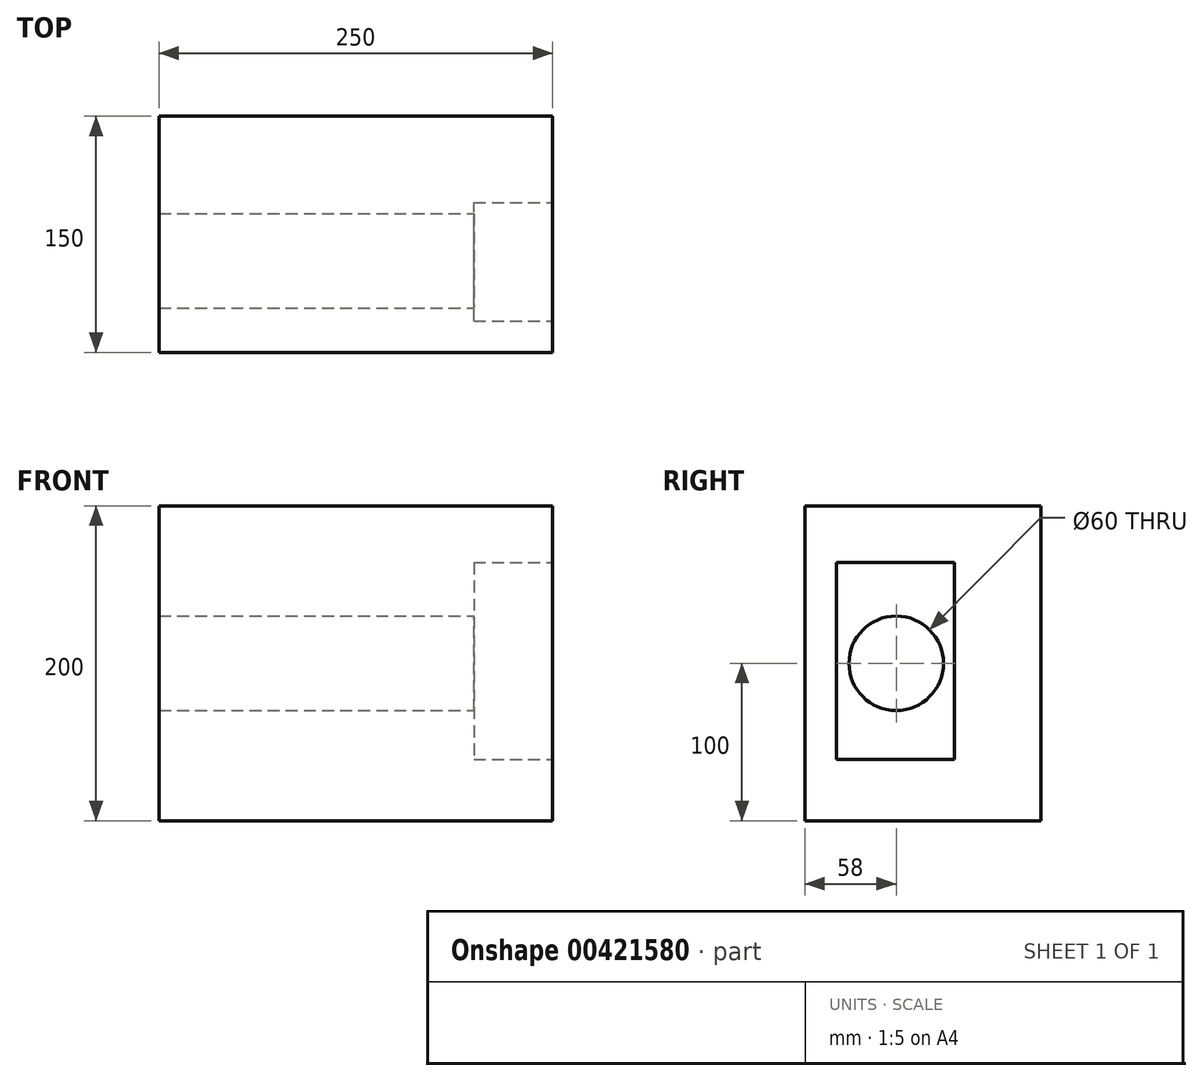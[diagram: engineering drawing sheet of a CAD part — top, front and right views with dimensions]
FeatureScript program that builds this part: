
annotation { "Feature Type Name" : "Feature", "Feature Type Description" : "" }
export const myFeature = defineFeature(function(context is Context, id is Id, definition is map)
    precondition{}
    {
        {
            var Q0;
            Q0=qCreatedBy(makeId("Front.planeOp"),FACE);
            var sketch = newSketch(context, id + "F0", { "sketchPlane" : qUnion([Q0])});
            skLineSegment(sketch, "E0.bottom", {"start": v(0, -31.1) * mm, "end": v(127.68, -31.1) * mm});
            skLineSegment(sketch, "E0.top", {"start": v(0, -82.4) * mm, "end": v(127.68, -82.4) * mm});
            skLineSegment(sketch, "E0.left", {"start": v(0, -31.1) * mm, "end": v(0, -82.4) * mm});
            skLineSegment(sketch, "E0.right", {"start": v(127.68, -31.1) * mm, "end": v(127.68, -82.4) * mm});
            skPoint(sketch, "E0.middle", {"position": v(63.84, -56.75) * mm});
            skSolve(sketch);
        }
        {
            var Q0;
            Q0=makeQuery(id+"F0.imprint","IMPRINT",FACE,{"disambiguationData":[TD([[makeQuery(id+"F0.imprint","IMPRINT",EDGE,{"derivedFrom":sQuery(id+"F0.wireOp",EDGE,"E0.bottom")}),-1.0]])]});
            extrude(context, id + "F1", {"entities" : qUnion([Q0]), "depth" : 114.37 * mm});
        }
        {
            var Q0;
            Q0=qCreatedBy(makeId("Front.planeOp"),FACE);
            var sketch = newSketch(context, id + "F2", { "sketchPlane" : qUnion([Q0])});
            skLineSegment(sketch, "E1", {"start": v(45.96, 141.6) * mm, "end": v(45.96, 90.77) * mm});
            skLineSegment(sketch, "E2", {"start": v(45.96, 90.77) * mm, "end": v(161.83, 90.77) * mm});
            skLineSegment(sketch, "E3", {"start": v(161.83, 90.77) * mm, "end": v(161.83, 141.6) * mm});
            skLineSegment(sketch, "E4", {"start": v(161.83, 141.6) * mm, "end": v(45.96, 141.6) * mm});
            skSolve(sketch);
        }
        {
            var Q0;
            Q0 = qSketchRegion(id + "F2", true);
            extrude(context, id + "F3", {"entities" : qUnion([Q0]), "depth" : 25 * mm, "offsetDistance" : 25 * mm});
        }
        {
            var Q0;
            Q0=makeQuery(id+"F3.opExtrude","CAP_FACE",FACE,{"disambiguationData":[OSD([sQuery(id+"F2.wireOp",EDGE,"E1"),sQuery(id+"F2.wireOp",EDGE,"E2"),sQuery(id+"F2.wireOp",EDGE,"E3"),sQuery(id+"F2.wireOp",EDGE,"E4")])],"isStart":false});
            extrude(context, id + "F4", {"entities" : qUnion([Q0]), "operationType" : NewBodyOperationType.ADD, "depth" : 30 * mm, "offsetDistance" : 25 * mm});
        }
        {
            var Q0;
            Q0=makeQuery(id+"F3.opExtrude","SWEPT_BODY",BODY,{"disambiguationData":[OSD([sQuery(id+"F2.wireOp",EDGE,"E1"),sQuery(id+"F2.wireOp",EDGE,"E2"),sQuery(id+"F2.wireOp",EDGE,"E3"),sQuery(id+"F2.wireOp",EDGE,"E4")])]});
            deleteBodies(context, id + "F5", {"entities" : qUnion([Q0])});
        }
        {
            var Q0;
            Q0=makeQuery(id+"F1.opExtrude","SWEPT_BODY",BODY,{"disambiguationData":[OSD([sQuery(id+"F0.wireOp",EDGE,"E0.bottom"),sQuery(id+"F0.wireOp",EDGE,"E0.top"),sQuery(id+"F0.wireOp",EDGE,"E0.left"),sQuery(id+"F0.wireOp",EDGE,"E0.right")])]});
            deleteBodies(context, id + "F6", {"entities" : qUnion([Q0])});
        }
        {
            var Q0;
            Q0=qCreatedBy(makeId("Front.planeOp"),FACE);
            var sketch = newSketch(context, id + "F7", { "sketchPlane" : qUnion([Q0])});
            skLineSegment(sketch, "E5.bottom", {"start": v(125, 100) * mm, "end": v(-125, 100) * mm});
            skLineSegment(sketch, "E5.top", {"start": v(125, -100) * mm, "end": v(-125, -100) * mm});
            skLineSegment(sketch, "E5.left", {"start": v(125, 100) * mm, "end": v(125, -100) * mm});
            skLineSegment(sketch, "E5.right", {"start": v(-125, 100) * mm, "end": v(-125, -100) * mm});
            skPoint(sketch, "E5.middle", {"position": v(0, 0) * mm});
            skSolve(sketch);
        }
        {
            var Q0;
            Q0=makeQuery(id+"F7.imprint","IMPRINT",FACE,{"disambiguationData":[TD([[makeQuery(id+"F7.imprint","IMPRINT",EDGE,{"derivedFrom":sQuery(id+"F7.wireOp",EDGE,"E5.bottom")}),1.0]])]});
            extrude(context, id + "F8", {"entities" : qUnion([Q0]), "depth" : 150 * mm, "offsetDistance" : 25 * mm});
        }
        {
            var Q0;
            Q0=makeQuery(id+"F8.opExtrude","SWEPT_FACE",FACE,{"disambiguationData":[OSD([sQuery(id+"F7.wireOp",EDGE,"E5.left")])]});
            var sketch = newSketch(context, id + "F9", { "sketchPlane" : qUnion([Q0])});
            skLineSegment(sketch, "E6.bottom", {"start": v(-130, 64) * mm, "end": v(-55, 64) * mm});
            skLineSegment(sketch, "E6.top", {"start": v(-130, -61) * mm, "end": v(-55, -61) * mm});
            skLineSegment(sketch, "E6.left", {"start": v(-130, 64) * mm, "end": v(-130, -61) * mm});
            skLineSegment(sketch, "E6.right", {"start": v(-55, 64) * mm, "end": v(-55, -61) * mm});
            skSolve(sketch);
        }
        {
            var Q0;
            Q0=makeQuery(id+"F9.imprint","IMPRINT",FACE,{"disambiguationData":[TD([[makeQuery(id+"F9.imprint","IMPRINT",EDGE,{"derivedFrom":sQuery(id+"F9.wireOp",EDGE,"E6.bottom")}),-1.0]])]});
            extrude(context, id + "F10", {"entities" : qUnion([Q0]), "operationType" : NewBodyOperationType.REMOVE, "oppositeDirection" : true, "depth" : 50 * mm, "offsetDistance" : 25 * mm});
        }
        {
            var Q0;
            Q0=makeQuery(id+"F10.boolean.opBoolean","COPY",FACE,{"derivedFrom":makeQuery(id+"F10.opExtrude","CAP_FACE",FACE,{"disambiguationData":[OSD([sQuery(id+"F9.wireOp",EDGE,"E6.bottom"),sQuery(id+"F9.wireOp",EDGE,"E6.top"),sQuery(id+"F9.wireOp",EDGE,"E6.left"),sQuery(id+"F9.wireOp",EDGE,"E6.right")])],"isStart":false})});
            var sketch = newSketch(context, id + "F11", { "sketchPlane" : qUnion([Q0])});
            skCircle(sketch, "E7", {"center": v(-92, 0) * mm, "radius": 30 * mm});
            skSolve(sketch);
        }
        {
            var Q0;
            Q0 = qSketchRegion(id + "F11", true);
            extrude(context, id + "F12", {"entities" : qUnion([Q0]), "operationType" : NewBodyOperationType.REMOVE, "endBound" : BoundingType.THROUGH_ALL, "oppositeDirection" : true, "depth" : 25 * mm, "offsetDistance" : 25 * mm});
        }
    });
